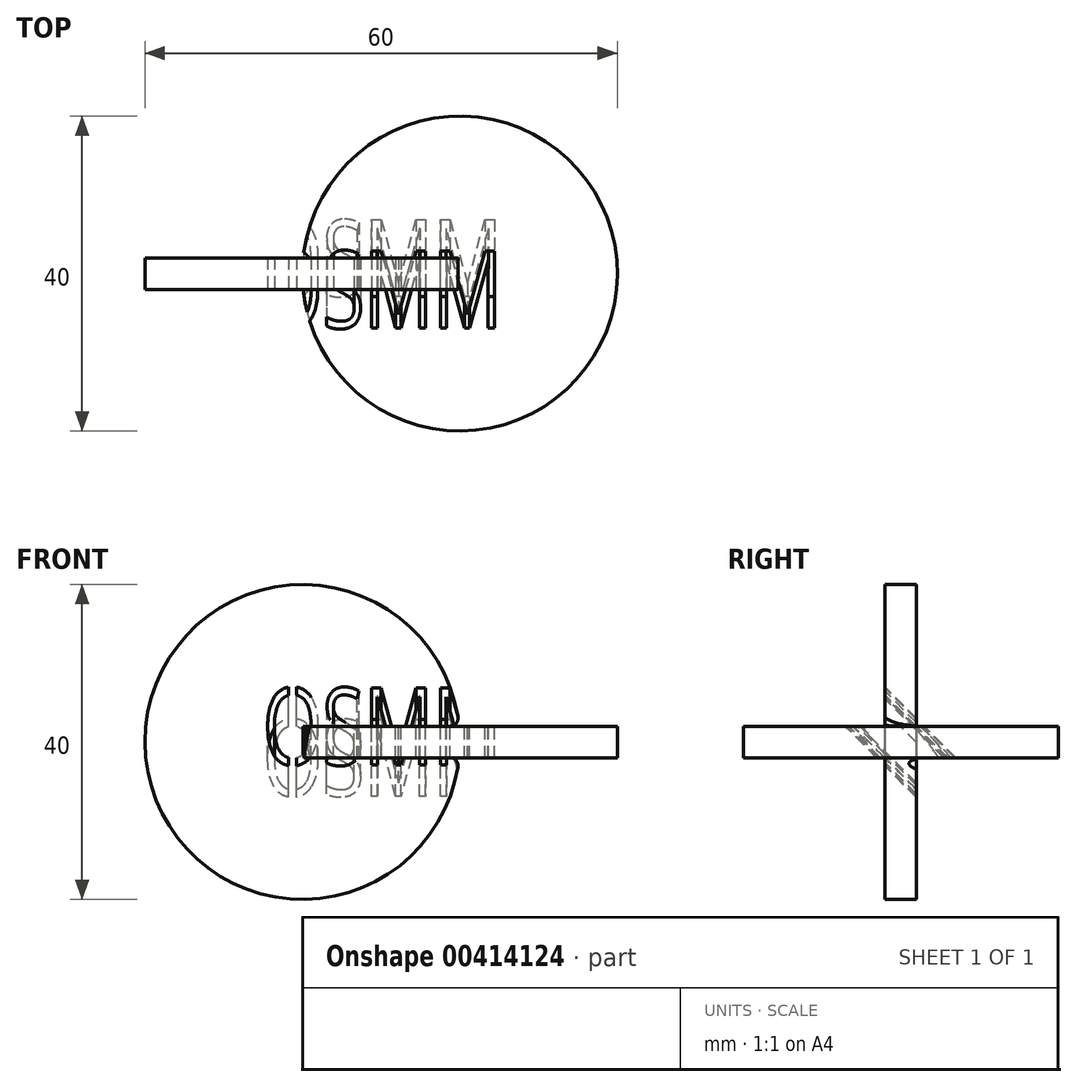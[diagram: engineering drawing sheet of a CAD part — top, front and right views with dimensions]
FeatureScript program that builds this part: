
annotation { "Feature Type Name" : "Feature", "Feature Type Description" : "" }
export const myFeature = defineFeature(function(context is Context, id is Id, definition is map)
    precondition{}
    {
        {
            assignVariable(context, id + "F0", {"name" : "material_thickness", "anyValue" : 4});
        }
        {
            var Q0;
            Q0=qCreatedBy(makeId("Front.planeOp"),FACE);
            var sketch = newSketch(context, id + "F1", { "sketchPlane" : qUnion([Q0])});
            skCircle(sketch, "E0", {"center": v(-10, 0) * mm, "radius": 20 * mm});
            skLineSegment(sketch, "E1", {"start": v(-10, 0) * mm, "end": v(10, 0) * mm, "construction": true});
            skLineSegment(sketch, "E2.bottom", {"start": v(0, 2) * mm, "end": v(20, 2) * mm});
            skLineSegment(sketch, "E2.top", {"start": v(0, -2) * mm, "end": v(20, -2) * mm});
            skLineSegment(sketch, "E2.left", {"start": v(0, 2) * mm, "end": v(0, -2) * mm});
            skLineSegment(sketch, "E2.right", {"start": v(20, 2) * mm, "end": v(20, -2) * mm});
            skPoint(sketch, "E2.middle", {"position": v(10, 0) * mm});
            skSolve(sketch);
        }
        {
            var Q0;
            {var subQ5=sQuery(id+"F1.wireOp",EDGE,"E2.left");Q0=makeQuery(id+"F1.imprint","IMPRINT",FACE,{"disambiguationData":[TD([[makeQuery(id+"F1.imprint","IMPRINT",EDGE,{"derivedFrom":subQ5}),-1.0]])]});}
            extrude(context, id + "F2", {"entities" : qUnion([Q0]), "endBound" : BoundingType.SYMMETRIC, "depth" : (getVariable(context, 'material_thickness')) * mm});
        }
        {
            var Q0;
            Q0=makeQuery(id+"F2.opExtrude","SWEPT_EDGE",EDGE,{"disambiguationData":[OSD([sQuery(id+"F1.wireOp",EDGE,"E0"),sQuery(id+"F1.wireOp",EDGE,"E2.bottom")])]});
            var Q1;
            Q1=makeQuery(id+"F2.opExtrude","SWEPT_EDGE",EDGE,{"disambiguationData":[OSD([sQuery(id+"F1.wireOp",EDGE,"E0"),sQuery(id+"F1.wireOp",EDGE,"E2.top")])]});
            fillet(context, id + "F3", {"entities" : qUnion([Q0, Q1]), "radius" : 1 * mm, "tangentPropagation" : true, "allowEdgeOverflow" : false});
        }
        {
            var Q0;
            Q0=qCreatedBy(makeId("Top.planeOp"),FACE);
            var sketch = newSketch(context, id + "F4", { "sketchPlane" : qUnion([Q0])});
            skCircle(sketch, "E3", {"center": v(10, 0) * mm, "radius": 20 * mm});
            skLineSegment(sketch, "E4", {"start": v(10, 0) * mm, "end": v(-10, 0) * mm, "construction": true});
            skLineSegment(sketch, "E5.bottom", {"start": v(0, -2) * mm, "end": v(-20, -2) * mm});
            skLineSegment(sketch, "E5.top", {"start": v(0, 2) * mm, "end": v(-20, 2) * mm});
            skLineSegment(sketch, "E5.left", {"start": v(0, -2) * mm, "end": v(0, 2) * mm});
            skLineSegment(sketch, "E5.right", {"start": v(-20, -2) * mm, "end": v(-20, 2) * mm});
            skPoint(sketch, "E5.middle", {"position": v(-10, 0) * mm});
            skSolve(sketch);
        }
        {
            var Q0;
            {var subQ5=sQuery(id+"F4.wireOp",EDGE,"E5.left");Q0=makeQuery(id+"F4.imprint","IMPRINT",FACE,{"disambiguationData":[TD([[makeQuery(id+"F4.imprint","IMPRINT",EDGE,{"derivedFrom":subQ5}),-1.0]])]});}
            extrude(context, id + "F5", {"entities" : qUnion([Q0]), "endBound" : BoundingType.SYMMETRIC, "depth" : (getVariable(context, 'material_thickness')) * mm});
        }
        {
            var Q0;
            Q0=makeQuery(id+"F5.opExtrude","CAP_EDGE",EDGE,{"disambiguationData":[OSD([sQuery(id+"F4.wireOp",EDGE,"E5.top")])],"isStart":true});
            cPlane(context, id + "F6", {"entities" : qUnion([Q0]), "cplaneType" : CPlaneType.LINE_ANGLE, "offset" : 25 * mm, "angle" : 45 * degree, "width" : 150 * mm, "height" : 150 * mm});
        }
        {
            var Q0;
            Q0=qCreatedBy(id+"F6.planeOp",FACE);
            var sketch = newSketch(context, id + "F7", { "sketchPlane" : qUnion([Q0])});
            skText(sketch, "E6", { "text": "OSMM", "fontName": "OpenSans-Regular.ttf"});
            skPoint(sketch, "E7.0", {"position": v(0, 0) * mm});
            skLineSegment(sketch, "E8", {"start": v(-10.75, -6.07) * mm, "end": v(-10.75, 5.93) * mm});
            skLineSegment(sketch, "E9", {"start": v(-11.75, -6.07) * mm, "end": v(-11.75, 5.93) * mm});
            skLineSegment(sketch, "E10", {"start": v(-10.75, 5.93) * mm, "end": v(-11.75, 5.93) * mm});
            skLineSegment(sketch, "E11", {"start": v(-10.75, -6.07) * mm, "end": v(-11.75, -6.07) * mm});
            const initialGuessF7  = {"E6": [-0.015, -0.00348, 1, 0, 0.00697]};
            skSetInitialGuess(sketch, initialGuessF7);
            skSolve(sketch);
        }
        {
            var Q0;
            {var subQ4=sQuery(id+"F7.wireOp",EDGE,"E6.sketch_text.stroke-3");Q0=makeQuery(id+"F7.imprint","IMPRINT",FACE,{"disambiguationData":[TD([[makeQuery(id+"F7.imprint","IMPRINT",EDGE,{"derivedFrom":subQ4}),-1.0]])]});}
            var Q1;
            {var subQ1=sQuery(id+"F7.wireOp",EDGE,"E6.sketch_text.stroke-0");Q1=makeQuery(id+"F7.imprint","IMPRINT",FACE,{"disambiguationData":[TD([[makeQuery(id+"F7.imprint","IMPRINT",EDGE,{"derivedFrom":subQ1}),-1.0]])]});}
            var Q2;
            Q2=makeQuery(id+"F7.imprint","IMPRINT",FACE,{"disambiguationData":[TD([[makeQuery(id+"F7.imprint","IMPRINT",EDGE,{"derivedFrom":sQuery(id+"F7.wireOp",EDGE,"E6.sketch_text.stroke-16")}),-1.0]])]});
            var Q3;
            Q3=makeQuery(id+"F7.imprint","IMPRINT",FACE,{"disambiguationData":[TD([[makeQuery(id+"F7.imprint","IMPRINT",EDGE,{"derivedFrom":sQuery(id+"F7.wireOp",EDGE,"E6.sketch_text.stroke-41")}),-1.0]])]});
            var Q4;
            Q4=makeQuery(id+"F7.imprint","IMPRINT",FACE,{"disambiguationData":[TD([[makeQuery(id+"F7.imprint","IMPRINT",EDGE,{"derivedFrom":sQuery(id+"F7.wireOp",EDGE,"E6.sketch_text.stroke-59")}),-1.0]])]});
            extrude(context, id + "F8", {"entities" : qUnion([Q0, Q1, Q2, Q3, Q4]), "operationType" : NewBodyOperationType.REMOVE, "endBound" : BoundingType.SYMMETRIC, "oppositeDirection" : true, "depth" : 50 * mm});
        }
    });
